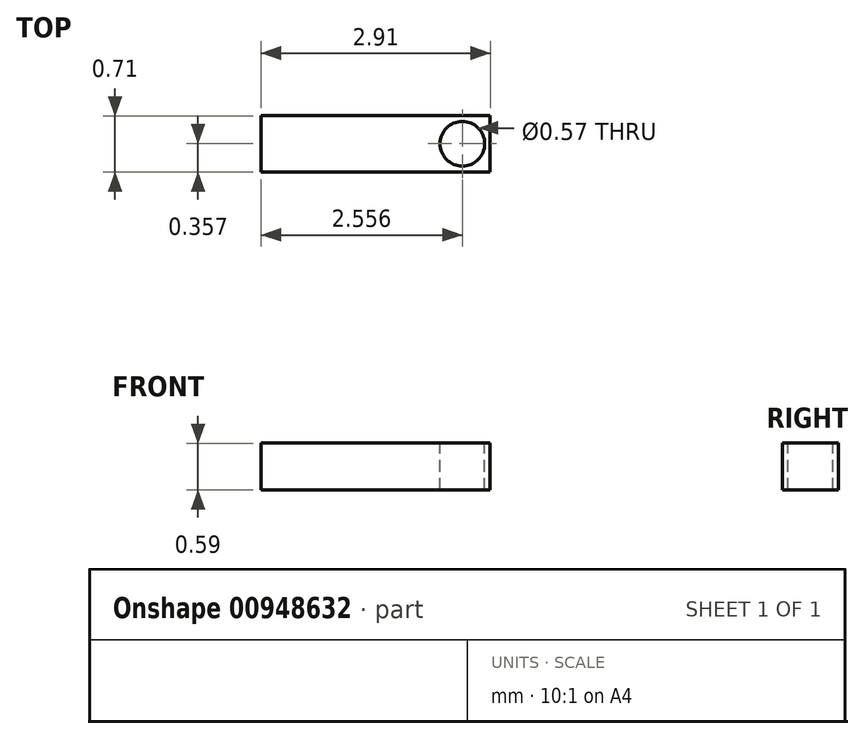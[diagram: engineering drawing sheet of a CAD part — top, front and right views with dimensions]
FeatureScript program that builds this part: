
annotation { "Feature Type Name" : "Feature", "Feature Type Description" : "" }
export const myFeature = defineFeature(function(context is Context, id is Id, definition is map)
    precondition{}
    {
        {
            var Q0;
            Q0=qCreatedBy(makeId("Front.planeOp"),FACE);
            var sketch = newSketch(context, id + "F0", { "sketchPlane" : qUnion([Q0])});
            skLineSegment(sketch, "E0.bottom", {"start": v(0, 0) * mm, "end": v(2.9, 0) * mm});
            skLineSegment(sketch, "E0.top", {"start": v(0, 0.6) * mm, "end": v(2.9, 0.6) * mm});
            skLineSegment(sketch, "E0.left", {"start": v(0, 0) * mm, "end": v(0, 0.6) * mm});
            skLineSegment(sketch, "E0.right", {"start": v(2.9, 0) * mm, "end": v(2.9, 0.6) * mm});
            skSolve(sketch);
        }
        {
            var Q0;
            Q0=makeQuery(id+"F0.imprint","IMPRINT",FACE,{"disambiguationData":[TD([[makeQuery(id+"F0.imprint","IMPRINT",EDGE,{"derivedFrom":sQuery(id+"F0.wireOp",EDGE,"E0.bottom")}),1.0]])]});
            extrude(context, id + "F1", {"entities" : qUnion([Q0]), "oppositeDirection" : true, "depth" : 0.71 * mm, "offsetDistance" : 25.4 * mm});
        }
        {
            var Q0;
            Q0=makeQuery(id+"F1.opExtrude","SWEPT_FACE",FACE,{"disambiguationData":[OSD([sQuery(id+"F0.wireOp",EDGE,"E0.top")])]});
            var sketch = newSketch(context, id + "F2", { "sketchPlane" : qUnion([Q0])});
            skCircle(sketch, "E1", {"center": v(2.56, 0.36) * mm, "radius": 0.28 * mm});
            skPoint(sketch, "E1.centerSnap0", {"position": v(2.9, 0.36) * mm});
            skSolve(sketch);
        }
        {
            var Q0;
            Q0=makeQuery(id+"F2.imprint","IMPRINT",FACE,{"disambiguationData":[TD([[makeQuery(id+"F2.imprint","IMPRINT",EDGE,{"derivedFrom":sQuery(id+"F2.wireOp",EDGE,"E1")}),1.0]])]});
            extrude(context, id + "F3", {"entities" : qUnion([Q0]), "operationType" : NewBodyOperationType.REMOVE, "oppositeDirection" : true, "depth" : 0.7 * mm, "offsetDistance" : 25.4 * mm});
        }
    });
